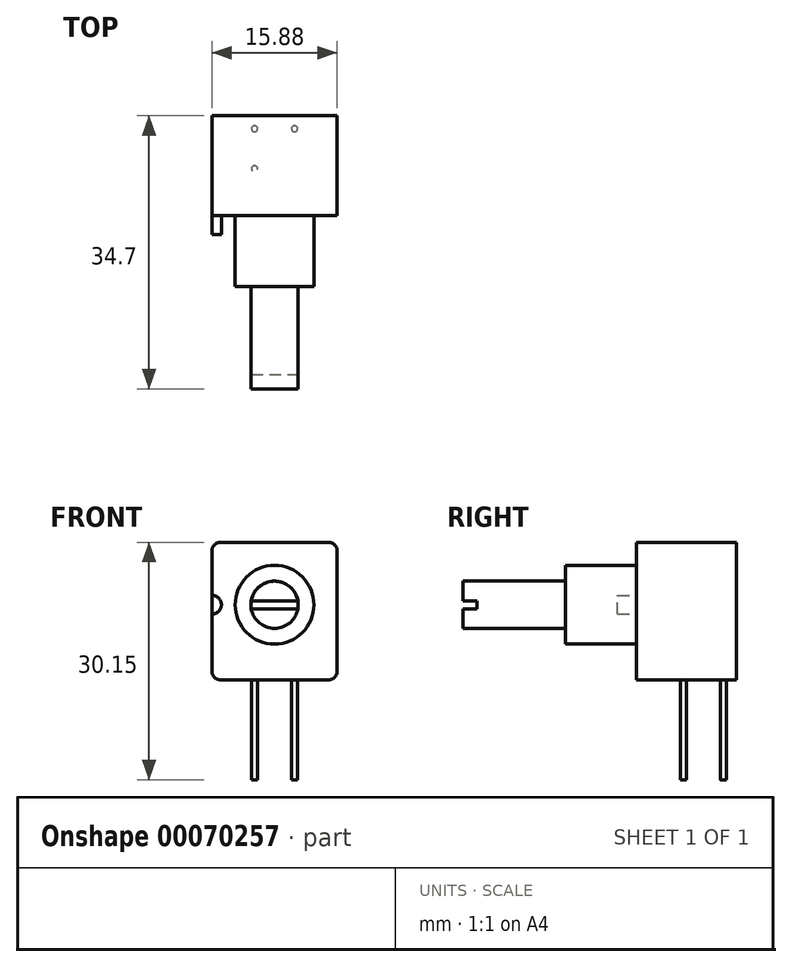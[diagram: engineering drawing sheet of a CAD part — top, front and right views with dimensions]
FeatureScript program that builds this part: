
annotation { "Feature Type Name" : "Feature", "Feature Type Description" : "" }
export const myFeature = defineFeature(function(context is Context, id is Id, definition is map)
    precondition{}
    {
        {
            var Q0;
            Q0=qCreatedBy(makeId("Front.planeOp"),FACE);
            var sketch = newSketch(context, id + "F0", { "sketchPlane" : qUnion([Q0])});
            skLineSegment(sketch, "E0.rect.bottom", {"start": v(6.94, -9.53) * mm, "end": v(-6.94, -9.53) * mm});
            skLineSegment(sketch, "E0.rect.top", {"start": v(6.94, 7.92) * mm, "end": v(-6.94, 7.92) * mm});
            skLineSegment(sketch, "E0.rect.left", {"start": v(7.94, -8.53) * mm, "end": v(7.94, 6.92) * mm});
            skLineSegment(sketch, "E0.rect.right", {"start": v(-7.94, -8.53) * mm, "end": v(-7.94, 6.92) * mm});
            skPoint(sketch, "E0.rect.middle", {"position": v(0, -0.8) * mm});
            skCircle(sketch, "E1", {"center": v(0, 0) * mm, "radius": 3 * mm});
            skCircle(sketch, "E2", {"center": v(0, 0) * mm, "radius": 5 * mm});
            skPoint(sketch, "E3.visualSharp", {"position": v(-7.94, 7.92) * mm});
            skArc(sketch, "E3.filletArc", {"start": v(-6.94, 7.92) * mm, "mid": v(-7.65, 7.63) * mm, "end": v(-7.94, 6.92) * mm});
            skPoint(sketch, "E4.visualSharp", {"position": v(7.94, 7.92) * mm});
            skArc(sketch, "E4.filletArc", {"start": v(7.94, 6.92) * mm, "mid": v(7.65, 7.63) * mm, "end": v(6.94, 7.92) * mm});
            skPoint(sketch, "E5.visualSharp", {"position": v(7.94, -9.53) * mm});
            skArc(sketch, "E5.filletArc", {"start": v(6.94, -9.53) * mm, "mid": v(7.65, -9.24) * mm, "end": v(7.94, -8.53) * mm});
            skPoint(sketch, "E6.visualSharp", {"position": v(-7.94, -9.53) * mm});
            skArc(sketch, "E6.filletArc", {"start": v(-7.94, -8.53) * mm, "mid": v(-7.65, -9.24) * mm, "end": v(-6.94, -9.53) * mm});
            skArc(sketch, "E7", {"start": v(-7.94, -1.19) * mm, "mid": v(-6.75, 0) * mm, "end": v(-7.94, 1.19) * mm});
            skLineSegment(sketch, "E8", {"start": v(-2.96, 0.5) * mm, "end": v(2.96, 0.5) * mm});
            skLineSegment(sketch, "E9.MirrorCS", {"start": v(-2.96, -0.5) * mm, "end": v(2.96, -0.5) * mm});
            skSolve(sketch);
        }
        {
            var Q0;
            Q0=makeQuery(id+"F0.imprint","IMPRINT",FACE,{"disambiguationData":[TD([[makeQuery(id+"F0.imprint","IMPRINT",EDGE,{"derivedFrom":sQuery(id+"F0.wireOp",EDGE,"E0.rect.bottom")}),-1.0]])]});
            var Q1;
            Q1=makeQuery(id+"F0.imprint","IMPRINT",FACE,{"disambiguationData":[TD([[makeQuery(id+"F0.imprint","IMPRINT",EDGE,{"derivedFrom":sQuery(id+"F0.wireOp",EDGE,"E2")}),1.0]])]});
            var Q2;
            {var subQ0=sQuery(id+"F0.wireOp",EDGE,"E7");Q2=makeQuery(id+"F0.imprint","IMPRINT",FACE,{"disambiguationData":[TD([[makeQuery(id+"F0.imprint","IMPRINT",EDGE,{"derivedFrom":subQ0}),1.0]])]});}
            var Q3;
            {var subQ0=sQuery(id+"F0.wireOp",EDGE,"E8");Q3=makeQuery(id+"F0.imprint","IMPRINT",FACE,{"disambiguationData":[TD([[makeQuery(id+"F0.imprint","IMPRINT",EDGE,{"derivedFrom":subQ0}),-1.0]])]});}
            var Q4;
            {var subQ0=sQuery(id+"F0.wireOp",EDGE,"E8");Q4=makeQuery(id+"F0.imprint","IMPRINT",FACE,{"disambiguationData":[TD([[makeQuery(id+"F0.imprint","IMPRINT",EDGE,{"derivedFrom":subQ0}),1.0]])]});}
            var Q5;
            {var subQ0=sQuery(id+"F0.wireOp",EDGE,"E9.MirrorCS");Q5=makeQuery(id+"F0.imprint","IMPRINT",FACE,{"disambiguationData":[TD([[makeQuery(id+"F0.imprint","IMPRINT",EDGE,{"derivedFrom":subQ0}),-1.0]])]});}
            extrude(context, id + "F1", {"entities" : qUnion([Q0, Q1, Q2, Q3, Q4, Q5]), "oppositeDirection" : true, "depth" : 12.7 * mm});
        }
        {
            var Q0;
            {var subQ0=sQuery(id+"F0.wireOp",EDGE,"E8");Q0=makeQuery(id+"F0.imprint","IMPRINT",FACE,{"disambiguationData":[TD([[makeQuery(id+"F0.imprint","IMPRINT",EDGE,{"derivedFrom":subQ0}),1.0]])]});}
            var Q1;
            {var subQ0=sQuery(id+"F0.wireOp",EDGE,"E9.MirrorCS");Q1=makeQuery(id+"F0.imprint","IMPRINT",FACE,{"disambiguationData":[TD([[makeQuery(id+"F0.imprint","IMPRINT",EDGE,{"derivedFrom":subQ0}),-1.0]])]});}
            extrude(context, id + "F2", {"entities" : qUnion([Q0, Q1]), "operationType" : NewBodyOperationType.ADD, "depth" : 22 * mm});
        }
        {
            var Q0;
            {var subQ0=sQuery(id+"F0.wireOp",EDGE,"E8");Q0=makeQuery(id+"F0.imprint","IMPRINT",FACE,{"disambiguationData":[TD([[makeQuery(id+"F0.imprint","IMPRINT",EDGE,{"derivedFrom":subQ0}),-1.0]])]});}
            extrude(context, id + "F3", {"entities" : qUnion([Q0]), "operationType" : NewBodyOperationType.ADD, "depth" : 20.2 * mm});
        }
        {
            var Q0;
            Q0=makeQuery(id+"F0.imprint","IMPRINT",FACE,{"disambiguationData":[TD([[makeQuery(id+"F0.imprint","IMPRINT",EDGE,{"derivedFrom":sQuery(id+"F0.wireOp",EDGE,"E2")}),1.0]])]});
            extrude(context, id + "F4", {"entities" : qUnion([Q0]), "operationType" : NewBodyOperationType.ADD, "depth" : 9 * mm});
        }
        {
            var Q0;
            {var subQ0=sQuery(id+"F0.wireOp",EDGE,"E7");Q0=makeQuery(id+"F0.imprint","IMPRINT",FACE,{"disambiguationData":[TD([[makeQuery(id+"F0.imprint","IMPRINT",EDGE,{"derivedFrom":subQ0}),1.0]])]});}
            extrude(context, id + "F5", {"entities" : qUnion([Q0]), "operationType" : NewBodyOperationType.ADD, "depth" : 2.36 * mm});
        }
        {
            var Q0;
            Q0=makeQuery(id+"F1.opExtrude","SWEPT_FACE",FACE,{"disambiguationData":[OSD([sQuery(id+"F0.wireOp",EDGE,"E0.rect.bottom")])]});
            var sketch = newSketch(context, id + "F6", { "sketchPlane" : qUnion([Q0])});
            skCircle(sketch, "E10", {"center": v(-2.54, -5.97) * mm, "radius": 0.38 * mm});
            skCircle(sketch, "E11", {"center": v(-2.54, -11.05) * mm, "radius": 0.38 * mm});
            skCircle(sketch, "E12", {"center": v(2.54, -11.05) * mm, "radius": 0.38 * mm});
            skSolve(sketch);
        }
        {
            var Q0;
            Q0 = qSketchRegion(id + "F6", true);
            extrude(context, id + "F7", {"entities" : qUnion([Q0]), "operationType" : NewBodyOperationType.ADD, "depth" : 12.7 * mm});
        }
    });
